# Revit family: OHMA
name_source: partatom
category: Mechanical Equipment
units: mm (PartAtom-declared; Revit-internal decimal feet)

## family parameters
Always vertical = Yes
Cut with Voids When Loaded = No
OmniClass Number = 23.40.40.11.17
OmniClass Title = Refrigerated Cases
Part Type = Normal
Room Calculation Point = No
Round Connector Dimension = Use Radius
Shared = No
Work Plane-Based = Yes

## types (4) — shared parameters
16" Shelf = Yes
18" Shelf = Yes
20" Shelf = Yes
24 hour Energy Usage (kWh) = 40.0 (kWh)
BOTTOM ELECTRICAL = Yes
BOTTOM REFRIGERATION PIPING = Yes
Certifications = NSF 7, UL471, CSA
Condensing  Data Volts = 208 V
Condensing Data  Phase = 1
Condensing Frequency (Hz) = 60 Hz
Cord Length = 120"
DATE = 05/20/2016
DESIGNERS NAME = SHIDDRAMESH
DRAIN PIPING = Yes
Default Elevation = 48"
Defrosts Per Day = 4
Description = Mobile High Multi-Deck Self-Contained Merchandiser
Discharge Air (°F) = 32 °F
Discharge Air Velocity (FPM) = 350 FPM
EQUIPMENT DESCRIPTION = Mobile High Multi-Deck Self-Contained Merchandiser
EQUIPMENT MARK = OHMA-NRG
GLASS = Glass
Height = 75 1/2"
High Power (Cornice) Amps = 0 A
Item Description = Mobile High Multi-Deck Self-Contained Merchandiser
LF STD END = Yes
Legend Number = OHMA-NRG
Light Length = 4'
Manufacturer = HILL PHOENIX
Model = OHMA-NRG
PAINTED METAL UPPER SHELF = PAINTED SHELVES
Plug Style = NEMA L14-20P
REAR REFRIGERATION PIPING = Yes
REFRIGERATION PIPING = COPPER PIPE
RT STD END = Yes
Refrigerant = R404A
STAINLESS STEEL = GALVANIZED STEEL
Standard Power Amps = 0 A
Suction Pressure @ Case Outlet (psig) (text) = 52-54  psi
Superheat Set Point @ Bulb (°F) = 6 - 8
System Data Phase = 1
System Data Volts = 208 V
Systems Frequency = 60 Hz
TOP ELECTRICAL = Yes
TOP REFRIGERATION PIPING = Yes
Timed-Off Defrost Fail-Safe (Min) = 60 (Min)
Timed-Off Defrost Termination Temp = 48 °F
URL = http://www.hillphoenix.com
Width = 43 1/4"

## per-type parameters (varying)
| type | CENTER LINE | Condensed Horsepower | DRAIN LINE | High Power (Cornice) Watts | Lbs. of Refrigerant | Length | Lights Per Row | Locked Rotor (LRA) Amps | Refgn | Running Load (RLA) Amps | Standard Power Watts |
| 4' | 24" | 3/4 | 24" | 22 W | 5 | 48" | 1 | 34 A | 22 1/2" | 6 A | 12 W |
| 6' | 36" |  | 36" | 0 W | 0 | 72" | 0 | 0 A | 28 5/8" | 0 A | 0 W |
| 8' | 48" |  | 48" | 0 W | 0 | 96" | 0 | 0 A | 28 5/8" | 0 A | 0 W |
| 12' | 72" |  | 72" | 0 W | 0 | 144" | 0 | 0 A | 28 5/8" | 0 A | 0 W |

## geometry (parser evidence)
native form markers: Blend x10, Sweep x2
no freeform markers — native parametric forms only
